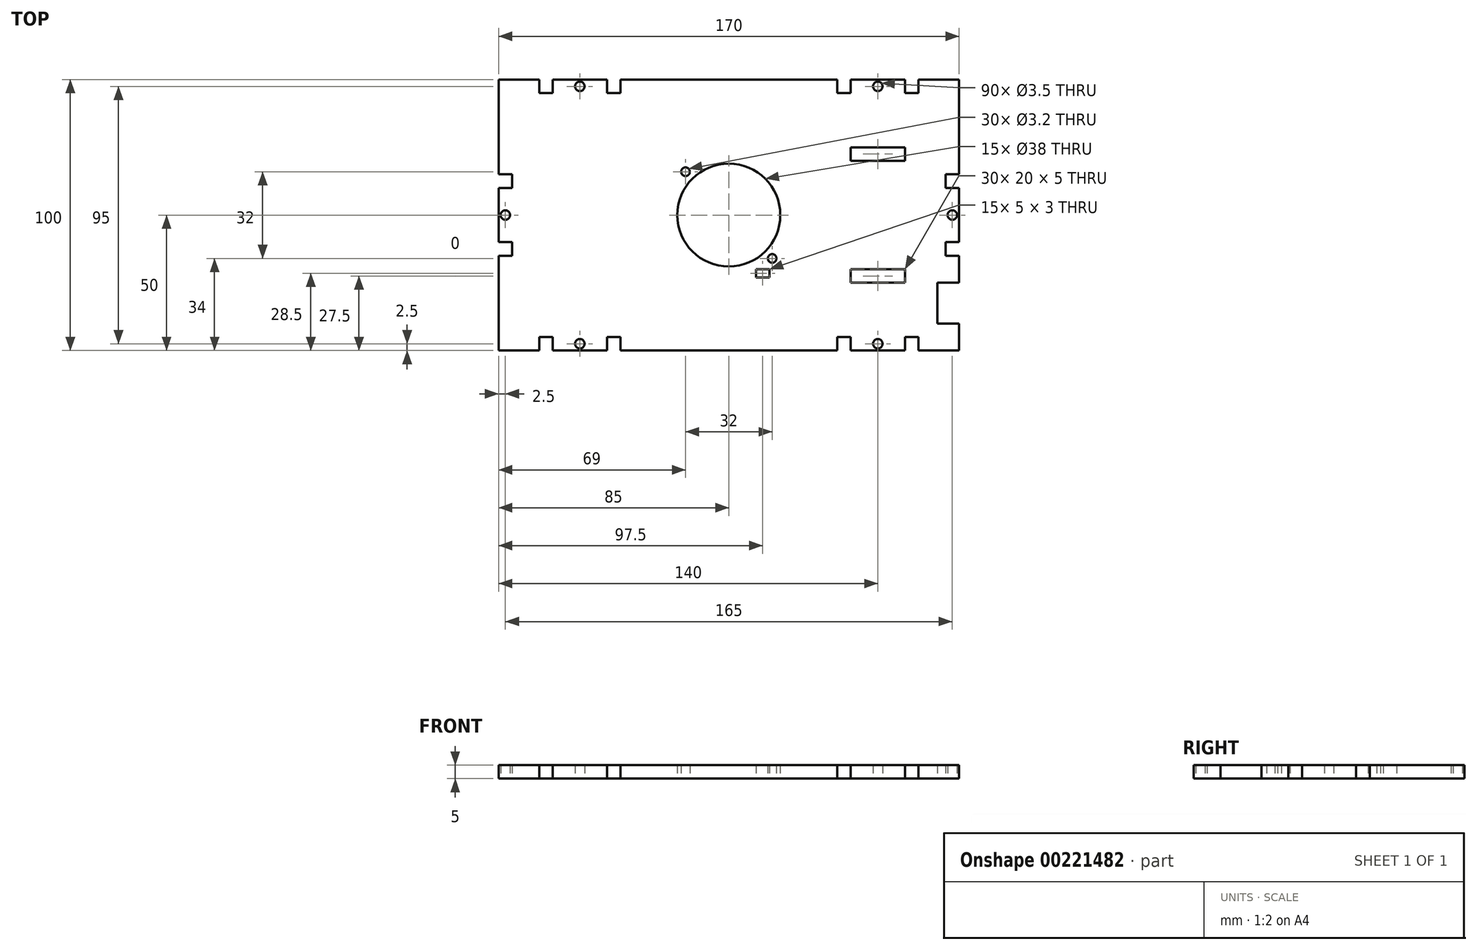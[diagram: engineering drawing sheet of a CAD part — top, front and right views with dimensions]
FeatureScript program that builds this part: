
annotation { "Feature Type Name" : "Feature", "Feature Type Description" : "" }
export const myFeature = defineFeature(function(context is Context, id is Id, definition is map)
    precondition{}
    {
        {
            var Q0;
            Q0=qCreatedBy(makeId("Top.planeOp"),FACE);
            var sketch = newSketch(context, id + "F0", { "sketchPlane" : qUnion([Q0])});
            skLineSegment(sketch, "E0.bottom", {"start": v(0, 100) * mm, "end": v(15, 100) * mm});
            skLineSegment(sketch, "E0.top", {"start": v(0, 0) * mm, "end": v(15, 0) * mm});
            skLineSegment(sketch, "E0.left", {"start": v(0, 100) * mm, "end": v(0, 65) * mm});
            skLineSegment(sketch, "E0.right", {"start": v(170, 100) * mm, "end": v(170, 65) * mm});
            skPoint(sketch, "E1", {"position": v(0, 50) * mm});
            skPoint(sketch, "E2", {"position": v(85, 100) * mm});
            skLineSegment(sketch, "E3.top", {"start": v(15, 5) * mm, "end": v(20, 5) * mm});
            skLineSegment(sketch, "E3.left", {"start": v(15, 0) * mm, "end": v(15, 5) * mm});
            skLineSegment(sketch, "E3.right", {"start": v(20, 0) * mm, "end": v(20, 5) * mm});
            skLineSegment(sketch, "E4.top", {"start": v(40, 5) * mm, "end": v(45, 5) * mm});
            skLineSegment(sketch, "E4.left", {"start": v(40, 0) * mm, "end": v(40, 5) * mm});
            skLineSegment(sketch, "E4.right", {"start": v(45, 0) * mm, "end": v(45, 5) * mm});
            skLineSegment(sketch, "E5.bottom", {"start": v(0, 35) * mm, "end": v(5, 35) * mm});
            skLineSegment(sketch, "E5.top", {"start": v(0, 40) * mm, "end": v(5, 40) * mm});
            skLineSegment(sketch, "E5.right", {"start": v(5, 35) * mm, "end": v(5, 40) * mm});
            skLineSegment(sketch, "E6.bottom", {"start": v(0, 60) * mm, "end": v(5, 60) * mm});
            skLineSegment(sketch, "E6.top", {"start": v(0, 65) * mm, "end": v(5, 65) * mm});
            skLineSegment(sketch, "E6.right", {"start": v(5, 60) * mm, "end": v(5, 65) * mm});
            skCircle(sketch, "E7", {"center": v(2.5, 50) * mm, "radius": 1.75 * mm});
            skPoint(sketch, "E7.centerSnap0", {"position": v(2.5, 60) * mm});
            skCircle(sketch, "E8", {"center": v(30, 2.5) * mm, "radius": 1.75 * mm});
            skLineSegment(sketch, "E9", {"start": v(85, 100) * mm, "end": v(85, 0) * mm, "construction": true});
            skPoint(sketch, "E9.endSnap0", {"position": v(85, 0) * mm});
            skLineSegment(sketch, "E10", {"start": v(170, 50) * mm, "end": v(0, 50) * mm, "construction": true});
            skLineSegment(sketch, "E11.MirrorCS", {"start": v(125, 0) * mm, "end": v(125, 5) * mm});
            skLineSegment(sketch, "E12.MirrorCS", {"start": v(130, 5) * mm, "end": v(125, 5) * mm});
            skLineSegment(sketch, "E13.MirrorCS", {"start": v(130, 0) * mm, "end": v(130, 5) * mm});
            skLineSegment(sketch, "E14.MirrorCS", {"start": v(155, 0) * mm, "end": v(155, 5) * mm});
            skLineSegment(sketch, "E15.MirrorCS", {"start": v(155, 5) * mm, "end": v(150, 5) * mm});
            skLineSegment(sketch, "E16.MirrorCS", {"start": v(150, 0) * mm, "end": v(150, 5) * mm});
            skCircle(sketch, "E17.MirrorC", {"center": v(140, 2.5) * mm, "radius": 1.75 * mm});
            skLineSegment(sketch, "E18.MirrorCS", {"start": v(170, 60) * mm, "end": v(165, 60) * mm});
            skLineSegment(sketch, "E19.MirrorCS", {"start": v(170, 65) * mm, "end": v(165, 65) * mm});
            skLineSegment(sketch, "E20.MirrorCS", {"start": v(165, 60) * mm, "end": v(165, 65) * mm});
            skCircle(sketch, "E21.MirrorC", {"center": v(167.5, 50) * mm, "radius": 1.75 * mm});
            skLineSegment(sketch, "E22.MirrorCS", {"start": v(165, 35) * mm, "end": v(165, 40) * mm});
            skLineSegment(sketch, "E23.MirrorCS", {"start": v(170, 40) * mm, "end": v(165, 40) * mm});
            skLineSegment(sketch, "E24.MirrorCS", {"start": v(170, 35) * mm, "end": v(165, 35) * mm});
            skLineSegment(sketch, "E25.MirrorCS", {"start": v(125, 100) * mm, "end": v(125, 95) * mm});
            skLineSegment(sketch, "E26.MirrorCS", {"start": v(130, 95) * mm, "end": v(125, 95) * mm});
            skLineSegment(sketch, "E27.MirrorCS", {"start": v(130, 100) * mm, "end": v(130, 95) * mm});
            skCircle(sketch, "E28.MirrorC", {"center": v(140, 97.5) * mm, "radius": 1.75 * mm});
            skLineSegment(sketch, "E29.MirrorCS", {"start": v(150, 100) * mm, "end": v(150, 95) * mm});
            skLineSegment(sketch, "E30.MirrorCS", {"start": v(155, 95) * mm, "end": v(150, 95) * mm});
            skLineSegment(sketch, "E31.MirrorCS", {"start": v(155, 100) * mm, "end": v(155, 95) * mm});
            skLineSegment(sketch, "E32.MirrorCS", {"start": v(45, 100) * mm, "end": v(45, 95) * mm});
            skLineSegment(sketch, "E33.MirrorCS", {"start": v(40, 100) * mm, "end": v(40, 95) * mm});
            skLineSegment(sketch, "E34.MirrorCS", {"start": v(40, 95) * mm, "end": v(45, 95) * mm});
            skCircle(sketch, "E35.MirrorC", {"center": v(30, 97.5) * mm, "radius": 1.75 * mm});
            skLineSegment(sketch, "E36.MirrorCS", {"start": v(20, 100) * mm, "end": v(20, 95) * mm});
            skLineSegment(sketch, "E37.MirrorCS", {"start": v(15, 95) * mm, "end": v(20, 95) * mm});
            skLineSegment(sketch, "E38.MirrorCS", {"start": v(15, 100) * mm, "end": v(15, 95) * mm});
            skLineSegment(sketch, "E39.trimOffspring", {"start": v(0, 35) * mm, "end": v(0, 0) * mm});
            skLineSegment(sketch, "E40.trimOffspring", {"start": v(0, 60) * mm, "end": v(0, 40) * mm});
            skLineSegment(sketch, "E41.trimOffspring", {"start": v(20, 0) * mm, "end": v(40, 0) * mm});
            skLineSegment(sketch, "E42.trimOffspring", {"start": v(45, 0) * mm, "end": v(125, 0) * mm});
            skLineSegment(sketch, "E43.trimOffspring", {"start": v(130, 0) * mm, "end": v(150, 0) * mm});
            skLineSegment(sketch, "E44.trimOffspring", {"start": v(155, 0) * mm, "end": v(170, 0) * mm});
            skLineSegment(sketch, "E45.trimOffspring", {"start": v(170, 35) * mm, "end": v(170, 25) * mm});
            skLineSegment(sketch, "E46.trimOffspring", {"start": v(170, 60) * mm, "end": v(170, 40) * mm});
            skLineSegment(sketch, "E47.trimOffspring", {"start": v(155, 100) * mm, "end": v(170, 100) * mm});
            skLineSegment(sketch, "E48.trimOffspring", {"start": v(130, 100) * mm, "end": v(150, 100) * mm});
            skLineSegment(sketch, "E49.trimOffspring", {"start": v(45, 100) * mm, "end": v(125, 100) * mm});
            skLineSegment(sketch, "E50.trimOffspring", {"start": v(20, 100) * mm, "end": v(40, 100) * mm});
            skLineSegment(sketch, "E51.bottom", {"start": v(130, 75) * mm, "end": v(150, 75) * mm});
            skLineSegment(sketch, "E51.top", {"start": v(130, 70) * mm, "end": v(150, 70) * mm});
            skLineSegment(sketch, "E51.left", {"start": v(130, 75) * mm, "end": v(130, 70) * mm});
            skLineSegment(sketch, "E51.right", {"start": v(150, 75) * mm, "end": v(150, 70) * mm});
            skLineSegment(sketch, "E52.MirrorCS", {"start": v(150, 25) * mm, "end": v(150, 30) * mm});
            skLineSegment(sketch, "E53.MirrorCS", {"start": v(130, 25) * mm, "end": v(150, 25) * mm});
            skLineSegment(sketch, "E54.MirrorCS", {"start": v(130, 25) * mm, "end": v(130, 30) * mm});
            skLineSegment(sketch, "E55.MirrorCS", {"start": v(130, 30) * mm, "end": v(150, 30) * mm});
            skLineSegment(sketch, "E56", {"start": v(170, 25) * mm, "end": v(162, 25) * mm});
            skLineSegment(sketch, "E57", {"start": v(162, 25) * mm, "end": v(162, 10) * mm});
            skLineSegment(sketch, "E58", {"start": v(162, 10) * mm, "end": v(170, 10) * mm});
            skLineSegment(sketch, "E59.trimOffspring", {"start": v(170, 10) * mm, "end": v(170, 0) * mm});
            skCircle(sketch, "E60", {"center": v(85, 50) * mm, "radius": 19 * mm});
            skLineSegment(sketch, "E61.bottom", {"start": v(69, 66) * mm, "end": v(101, 66) * mm, "construction": true});
            skLineSegment(sketch, "E61.top", {"start": v(69, 34) * mm, "end": v(101, 34) * mm, "construction": true});
            skLineSegment(sketch, "E61.left", {"start": v(69, 66) * mm, "end": v(69, 34) * mm, "construction": true});
            skLineSegment(sketch, "E61.right", {"start": v(101, 66) * mm, "end": v(101, 34) * mm, "construction": true});
            skPoint(sketch, "E62", {"position": v(85, 66) * mm});
            skPoint(sketch, "E63", {"position": v(69, 50) * mm});
            skCircle(sketch, "E64", {"center": v(69, 66) * mm, "radius": 1.6 * mm});
            skCircle(sketch, "E65", {"center": v(101, 34) * mm, "radius": 1.6 * mm});
            skLineSegment(sketch, "E66.bottom", {"start": v(65, 70) * mm, "end": v(105, 70) * mm, "construction": true});
            skLineSegment(sketch, "E66.top", {"start": v(65, 30) * mm, "end": v(105, 30) * mm, "construction": true});
            skLineSegment(sketch, "E66.left", {"start": v(65, 70) * mm, "end": v(65, 30) * mm, "construction": true});
            skLineSegment(sketch, "E66.right", {"start": v(105, 70) * mm, "end": v(105, 30) * mm, "construction": true});
            skPoint(sketch, "E67", {"position": v(85, 70) * mm});
            skPoint(sketch, "E68", {"position": v(105, 50) * mm});
            skLineSegment(sketch, "E69.bottom", {"start": v(95, 30) * mm, "end": v(100, 30) * mm});
            skLineSegment(sketch, "E69.top", {"start": v(95, 27) * mm, "end": v(100, 27) * mm});
            skLineSegment(sketch, "E69.left", {"start": v(95, 30) * mm, "end": v(95, 27) * mm});
            skLineSegment(sketch, "E69.right", {"start": v(100, 30) * mm, "end": v(100, 27) * mm});
            skSolve(sketch);
        }
        {
            var Q0;
            Q0=makeQuery(id+"F0.imprint","IMPRINT",FACE,{"disambiguationData":[TD([[makeQuery(id+"F0.imprint","IMPRINT",EDGE,{"derivedFrom":sQuery(id+"F0.wireOp",EDGE,"E0.bottom")}),-1.0]])]});
            extrude(context, id + "F1", {"entities" : qUnion([Q0]), "depth" : 5 * mm});
        }
    });
